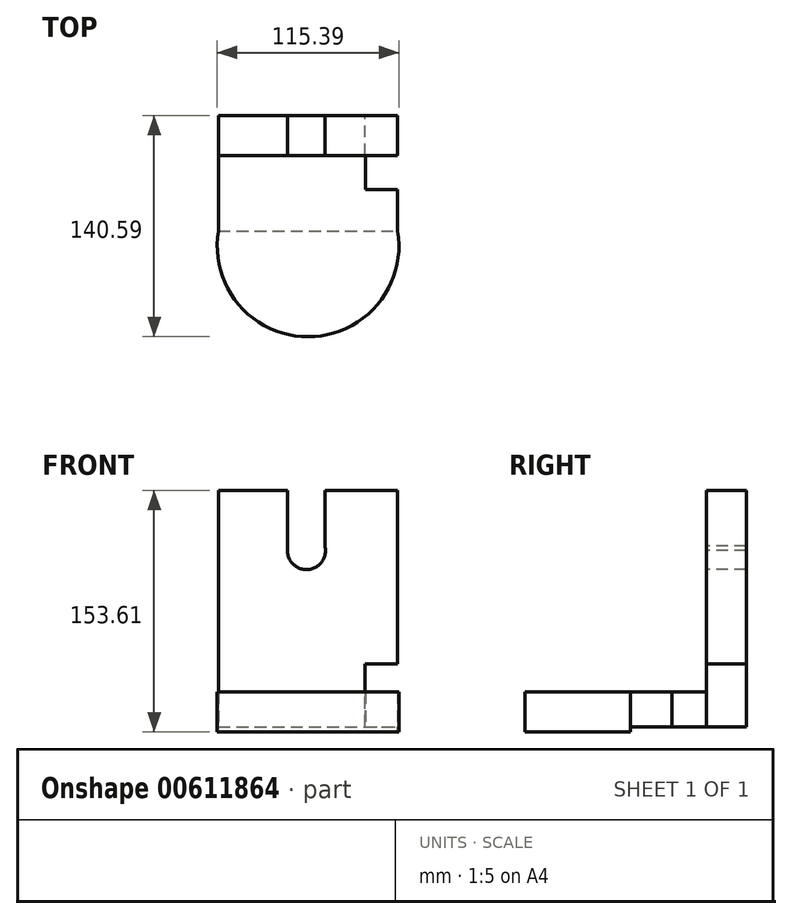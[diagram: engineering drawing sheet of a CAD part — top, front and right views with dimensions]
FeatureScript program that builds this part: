
annotation { "Feature Type Name" : "Feature", "Feature Type Description" : "" }
export const myFeature = defineFeature(function(context is Context, id is Id, definition is map)
    precondition{}
    {
        {
            var Q0;
            Q0=qCreatedBy(makeId("Front.planeOp"),FACE);
            var sketch = newSketch(context, id + "F0", { "sketchPlane" : qUnion([Q0])});
            skLineSegment(sketch, "E0.bottom", {"start": v(-58.38, -76.07) * mm, "end": v(55.26, -76.07) * mm});
            skLineSegment(sketch, "E0.top", {"start": v(-58.38, 74.24) * mm, "end": v(55.26, 74.24) * mm});
            skLineSegment(sketch, "E0.left", {"start": v(-58.38, -76.07) * mm, "end": v(-58.38, 74.24) * mm});
            skLineSegment(sketch, "E0.right", {"start": v(55.26, -76.07) * mm, "end": v(55.26, 74.24) * mm});
            skSolve(sketch);
        }
        {
            var Q0;
            Q0=makeQuery(id+"F0.imprint","IMPRINT",FACE,{"disambiguationData":[TD([[makeQuery(id+"F0.imprint","IMPRINT",EDGE,{"derivedFrom":sQuery(id+"F0.wireOp",EDGE,"E0.bottom")}),1.0]])]});
            extrude(context, id + "F1", {"entities" : qUnion([Q0]), "depth" : 25.4 * mm, "offsetDistance" : 25.4 * mm});
        }
        {
            var Q0;
            Q0=makeQuery(id+"F1.opExtrude","SWEPT_FACE",FACE,{"disambiguationData":[OSD([sQuery(id+"F0.wireOp",EDGE,"E0.bottom")])]});
            var sketch = newSketch(context, id + "F2", { "sketchPlane" : qUnion([Q0])});
            skLineSegment(sketch, "E1.bottom", {"start": v(-58.38, 25.4) * mm, "end": v(55.45, 25.4) * mm});
            skLineSegment(sketch, "E1.top", {"start": v(-58.38, 48.02) * mm, "end": v(55.45, 48.02) * mm});
            skLineSegment(sketch, "E1.left", {"start": v(-58.38, 25.4) * mm, "end": v(-58.38, 48.02) * mm});
            skLineSegment(sketch, "E1.right", {"start": v(55.45, 25.4) * mm, "end": v(55.45, 48.02) * mm});
            skSolve(sketch);
        }
        {
            var Q0;
            Q0=makeQuery(id+"F2.imprint","IMPRINT",FACE,{"disambiguationData":[TD([[makeQuery(id+"F2.imprint","IMPRINT",EDGE,{"derivedFrom":sQuery(id+"F2.wireOp",EDGE,"E1.top")}),-1.0]])]});
            extrude(context, id + "F3", {"entities" : qUnion([Q0]), "oppositeDirection" : true, "depth" : 22.1 * mm, "offsetDistance" : 25.4 * mm});
        }
        {
            var Q0;
            Q0=makeQuery(id+"F3.opExtrude","SWEPT_FACE",FACE,{"disambiguationData":[OSD([sQuery(id+"F2.wireOp",EDGE,"E1.top")])]});
            extrude(context, id + "F4", {"entities" : qUnion([Q0]), "operationType" : NewBodyOperationType.ADD, "depth" : 25.4 * mm, "offsetDistance" : 25.4 * mm});
        }
        {
            var Q0;
            {var subQ0=sQuery(id+"F2.wireOp",EDGE,"E1.right");Q0=makeQuery(id+"F4.boolean.opBoolean","MERGE",FACE,{"derivedFrom":[makeQuery(id+"F3.opExtrude","SWEPT_FACE",FACE,{"disambiguationData":[OSD([subQ0])]}),makeQuery(id+"F4.opExtrude","SWEPT_FACE",FACE,{"disambiguationData":[OSD([sQuery(id+"F2.wireOp",EDGE,"E1.top"),subQ0])]})]});}
            var sketch = newSketch(context, id + "F5", { "sketchPlane" : qUnion([Q0])});
            skLineSegment(sketch, "E2.bottom", {"start": v(-48.2, -36.14) * mm, "end": v(7.27, -36.14) * mm});
            skLineSegment(sketch, "E2.top", {"start": v(-48.2, -83.45) * mm, "end": v(7.27, -83.45) * mm});
            skLineSegment(sketch, "E2.left", {"start": v(-48.2, -36.14) * mm, "end": v(-48.2, -83.45) * mm});
            skLineSegment(sketch, "E2.right", {"start": v(7.27, -36.14) * mm, "end": v(7.27, -83.45) * mm});
            skSolve(sketch);
        }
        {
            var Q0;
            {var subQ6=sQuery(id+"F5.wireOp",EDGE,"E2.bottom");Q0=makeQuery(id+"F5.imprint","IMPRINT",FACE,{"disambiguationData":[TD([[makeQuery(id+"F5.imprint","IMPRINT",EDGE,{"derivedFrom":subQ6}),-1.0]])]});}
            extrude(context, id + "F6", {"entities" : qUnion([Q0]), "operationType" : NewBodyOperationType.REMOVE, "oppositeDirection" : true, "depth" : 20.83 * mm, "offsetDistance" : 25.4 * mm});
        }
        {
            var Q0;
            {var subQ0=sQuery(id+"F2.wireOp",EDGE,"E1.right");Q0=makeQuery(id+"F4.boolean.opBoolean","MERGE",FACE,{"derivedFrom":[makeQuery(id+"F3.opExtrude","SWEPT_FACE",FACE,{"disambiguationData":[OSD([subQ0])]}),makeQuery(id+"F4.opExtrude","SWEPT_FACE",FACE,{"disambiguationData":[OSD([sQuery(id+"F2.wireOp",EDGE,"E1.top"),subQ0])]})]});}
            var sketch = newSketch(context, id + "F7", { "sketchPlane" : qUnion([Q0])});
            skLineSegment(sketch, "E3.bottom", {"start": v(-23, -49.67) * mm, "end": v(-47.2, -49.67) * mm});
            skLineSegment(sketch, "E3.top", {"start": v(-23, -78.82) * mm, "end": v(-47.2, -78.82) * mm});
            skLineSegment(sketch, "E3.left", {"start": v(-23, -49.67) * mm, "end": v(-23, -78.82) * mm});
            skLineSegment(sketch, "E3.right", {"start": v(-47.2, -49.67) * mm, "end": v(-47.2, -78.82) * mm});
            skSolve(sketch);
        }
        {
            var Q0;
            {var subQ1=sQuery(id+"F2.wireOp",EDGE,"E1.right");var subQ7=makeQuery(id+"F3.opExtrude","SWEPT_EDGE",EDGE,{"disambiguationData":[OSD([sQuery(id+"F2.wireOp",EDGE,"E1.bottom"),subQ1])]});Q0=makeQuery(id+"F7.imprint","IMPRINT",FACE,{"disambiguationData":[TD([[makeQuery(id+"F7.imprint","IMPRINT",EDGE,{"derivedFrom":subQ7}),-1.0]])]});}
            extrude(context, id + "F8", {"entities" : qUnion([Q0]), "operationType" : NewBodyOperationType.REMOVE, "oppositeDirection" : true, "depth" : 20.57 * mm, "offsetDistance" : 25.4 * mm});
        }
        {
            var Q0;
            Q0=makeQuery(id+"F1.opExtrude","CAP_FACE",FACE,{"disambiguationData":[OSD([sQuery(id+"F0.wireOp",EDGE,"E0.bottom"),sQuery(id+"F0.wireOp",EDGE,"E0.top"),sQuery(id+"F0.wireOp",EDGE,"E0.left"),sQuery(id+"F0.wireOp",EDGE,"E0.right")])],"isStart":false});
            var sketch = newSketch(context, id + "F9", { "sketchPlane" : qUnion([Q0])});
            skCircle(sketch, "E4", {"center": v(-2.47, 35.93) * mm, "radius": 12.09 * mm});
            skLineSegment(sketch, "E5.bottom", {"start": v(-2.47, 35.93) * mm, "end": v(-14.76, 35.93) * mm});
            skLineSegment(sketch, "E5.top", {"start": v(-2.47, 74.24) * mm, "end": v(-14.76, 74.24) * mm});
            skLineSegment(sketch, "E5.left", {"start": v(-2.47, 35.93) * mm, "end": v(-2.47, 74.24) * mm});
            skLineSegment(sketch, "E5.right", {"start": v(-14.76, 35.93) * mm, "end": v(-14.76, 74.24) * mm});
            skLineSegment(sketch, "E6.bottom", {"start": v(-2.47, 35.93) * mm, "end": v(9.8, 35.93) * mm});
            skLineSegment(sketch, "E6.top", {"start": v(-2.47, 74.24) * mm, "end": v(9.8, 74.24) * mm});
            skLineSegment(sketch, "E6.right", {"start": v(9.8, 35.93) * mm, "end": v(9.8, 74.24) * mm});
            skSolve(sketch);
        }
        {
            var Q0;
            Q0=makeQuery(id+"F9.imprint","IMPRINT",FACE,{"disambiguationData":[TD([[makeQuery(id+"F9.imprint","IMPRINT",EDGE,{"derivedFrom":sQuery(id+"F9.wireOp",EDGE,"E4")}),1.0]])]});
            extrude(context, id + "F10", {"entities" : qUnion([Q0]), "operationType" : NewBodyOperationType.REMOVE, "oppositeDirection" : true, "depth" : 50.8 * mm, "offsetDistance" : 25.4 * mm});
        }
        {
            var Q0;
            Q0=makeQuery(id+"F1.opExtrude","CAP_FACE",FACE,{"disambiguationData":[OSD([sQuery(id+"F0.wireOp",EDGE,"E0.bottom"),sQuery(id+"F0.wireOp",EDGE,"E0.top"),sQuery(id+"F0.wireOp",EDGE,"E0.left"),sQuery(id+"F0.wireOp",EDGE,"E0.right")])],"isStart":false});
            var sketch = newSketch(context, id + "F11", { "sketchPlane" : qUnion([Q0])});
            skLineSegment(sketch, "E7.bottom", {"start": v(-2.47, 35.93) * mm, "end": v(-14.57, 35.93) * mm});
            skLineSegment(sketch, "E7.top", {"start": v(-2.47, 74.24) * mm, "end": v(-14.57, 74.24) * mm});
            skLineSegment(sketch, "E7.left", {"start": v(-2.47, 35.93) * mm, "end": v(-2.47, 74.24) * mm});
            skLineSegment(sketch, "E7.right", {"start": v(-14.57, 35.93) * mm, "end": v(-14.57, 74.24) * mm});
            skLineSegment(sketch, "E8.bottom", {"start": v(-2.47, 35.93) * mm, "end": v(9.26, 35.93) * mm});
            skLineSegment(sketch, "E8.top", {"start": v(-2.47, 74.24) * mm, "end": v(9.26, 74.24) * mm});
            skLineSegment(sketch, "E8.right", {"start": v(9.26, 35.93) * mm, "end": v(9.26, 74.24) * mm});
            skSolve(sketch);
        }
        {
            var Q0;
            {var subQ2=sQuery(id+"F11.wireOp",EDGE,"E7.top");Q0=makeQuery(id+"F11.imprint","IMPRINT",FACE,{"disambiguationData":[TD([[makeQuery(id+"F11.imprint","IMPRINT",EDGE,{"derivedFrom":subQ2}),-1.0]])]});}
            extrude(context, id + "F12", {"entities" : qUnion([Q0]), "operationType" : NewBodyOperationType.REMOVE, "oppositeDirection" : true, "depth" : 25.4 * mm, "offsetDistance" : 25.4 * mm});
        }
        {
            var Q0;
            Q0 = qSketchRegion(id + "F11", true);
            extrude(context, id + "F13", {"entities" : qUnion([Q0]), "operationType" : NewBodyOperationType.REMOVE, "oppositeDirection" : true, "depth" : 25.4 * mm, "offsetDistance" : 25.4 * mm});
        }
        {
            var Q0;
            {var subQ0=sQuery(id+"F2.wireOp",EDGE,"E1.top");Q0=makeQuery(id+"F4.boolean.opBoolean","MERGE",FACE,{"derivedFrom":[makeQuery(id+"F3.opExtrude","CAP_FACE",FACE,{"disambiguationData":[OSD([sQuery(id+"F2.wireOp",EDGE,"E1.bottom"),subQ0,sQuery(id+"F2.wireOp",EDGE,"E1.left"),sQuery(id+"F2.wireOp",EDGE,"E1.right")])],"isStart":false}),makeQuery(id+"F4.opExtrude","SWEPT_FACE",FACE,{"disambiguationData":[OSD([subQ0]),TDD([makeQuery(id+"F3.opExtrude","CAP_EDGE",EDGE,{"disambiguationData":[OSD([subQ0])],"isStart":false})])]})]});}
            var sketch = newSketch(context, id + "F14", { "sketchPlane" : qUnion([Q0])});
            skArc(sketch, "E9", {"start": v(-58.38, -73.42) * mm, "mid": v(-1.47, -140.59) * mm, "end": v(55.45, -73.42) * mm});
            skPoint(sketch, "E9.first.point", {"position": v(-58.38, -73.42) * mm});
            skPoint(sketch, "E9.second.point", {"position": v(55.45, -73.42) * mm});
            skPoint(sketch, "E9.third.point", {"position": v(-6.31, -25.4) * mm});
            skSolve(sketch);
        }
        {
            var Q0;
            Q0=makeQuery(id+"F14.imprint","IMPRINT",FACE,{"disambiguationData":[TD([[makeQuery(id+"F14.imprint","IMPRINT",EDGE,{"derivedFrom":sQuery(id+"F14.wireOp",EDGE,"E9")}),1.0]])]});
            extrude(context, id + "F15", {"entities" : qUnion([Q0]), "operationType" : NewBodyOperationType.ADD, "oppositeDirection" : true, "depth" : 25.4 * mm, "offsetDistance" : 25.4 * mm});
        }
    });
